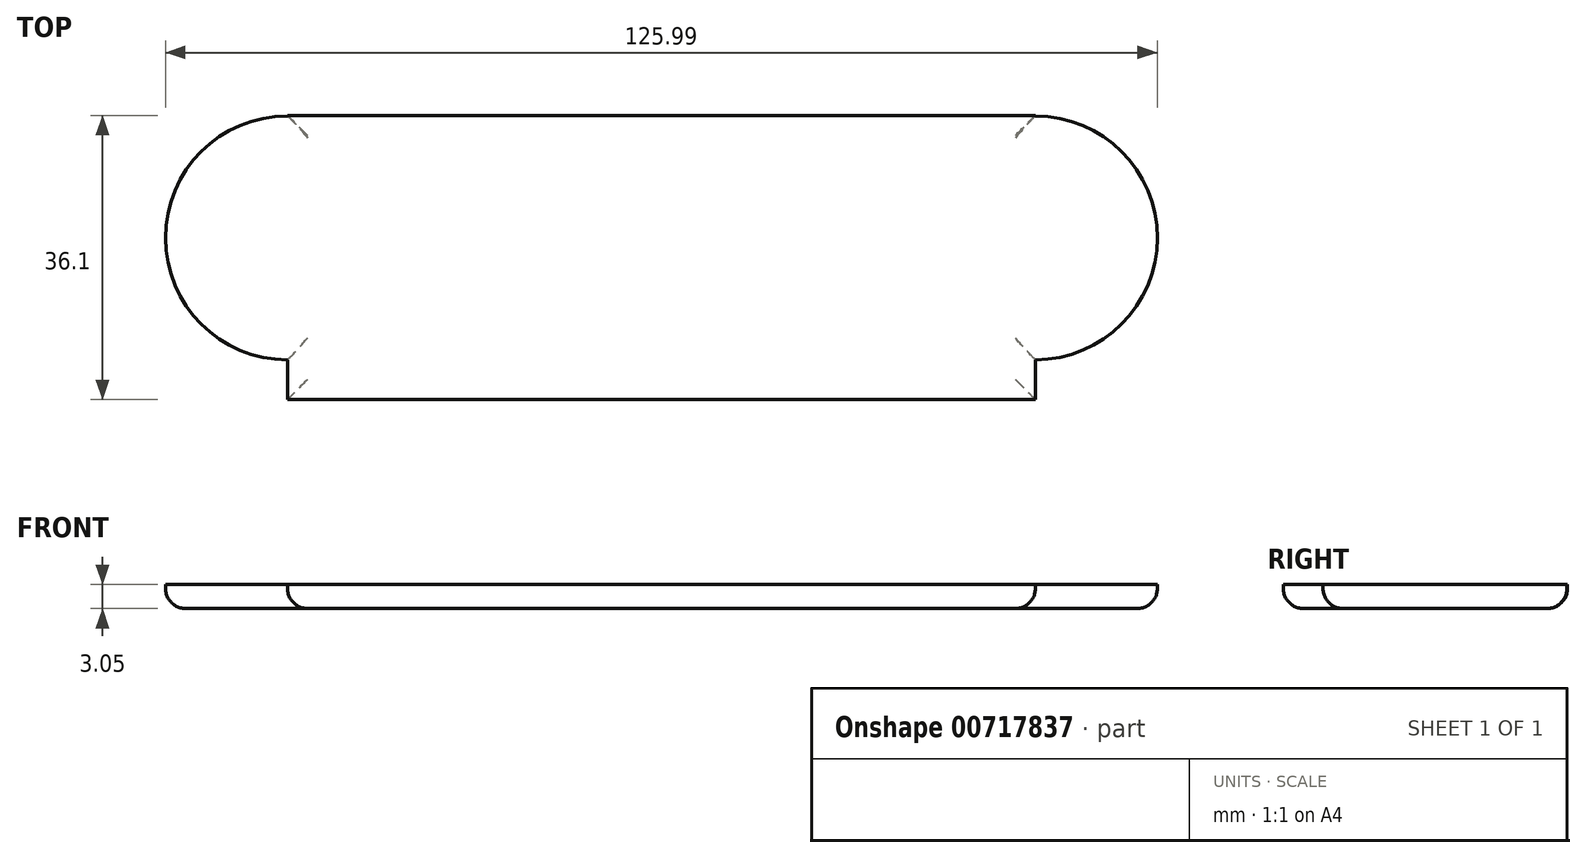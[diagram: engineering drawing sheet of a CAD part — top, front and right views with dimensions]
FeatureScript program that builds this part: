
annotation { "Feature Type Name" : "Feature", "Feature Type Description" : "" }
export const myFeature = defineFeature(function(context is Context, id is Id, definition is map)
    precondition{}
    {
        {
            var Q0;
            Q0=qCreatedBy(makeId("Top.planeOp"),FACE);
            var sketch = newSketch(context, id + "F0", { "sketchPlane" : qUnion([Q0])});
            skLineSegment(sketch, "E0.bottom", {"start": v(47.5, 18.05) * mm, "end": v(-47.5, 18.05) * mm});
            skLineSegment(sketch, "E0.top", {"start": v(47.5, -18.05) * mm, "end": v(-47.5, -18.05) * mm});
            skLineSegment(sketch, "E0.left", {"start": v(47.5, 18.05) * mm, "end": v(47.5, -18.05) * mm});
            skLineSegment(sketch, "E0.right", {"start": v(-47.5, 18.05) * mm, "end": v(-47.5, -18.05) * mm});
            skPoint(sketch, "E0.middle", {"position": v(0, 0) * mm});
            skCircle(sketch, "E1", {"center": v(-47.5, 2.49) * mm, "radius": 15.5 * mm});
            skCircle(sketch, "E2", {"center": v(47.5, 2.49) * mm, "radius": 15.5 * mm});
            skSolve(sketch);
        }
        {
            var Q0;
            Q0=qSketchRegion(id+"F0",true);
            extrude(context, id + "F1", {"entities" : qUnion([Q0]), "oppositeDirection" : true, "depth" : 3.05 * mm, "offsetDistance" : 25.4 * mm});
        }
        {
            var Q0;
            Q0=makeQuery(id+"F1.opExtrude","CAP_EDGE",EDGE,{"disambiguationData":[OSD([sQuery(id+"F0.wireOp",EDGE,"E1")])],"isStart":false});
            var Q1;
            Q1=makeQuery(id+"F1.opExtrude","CAP_EDGE",EDGE,{"disambiguationData":[OSD([sQuery(id+"F0.wireOp",EDGE,"E2")])],"isStart":false});
            var Q2;
            Q2=makeQuery(id+"F1.opExtrude","CAP_FACE",FACE,{"disambiguationData":[OSD([sQuery(id+"F0.wireOp",EDGE,"E0.bottom"),sQuery(id+"F0.wireOp",EDGE,"E0.top"),sQuery(id+"F0.wireOp",EDGE,"E0.left"),sQuery(id+"F0.wireOp",EDGE,"E0.right"),sQuery(id+"F0.wireOp",EDGE,"E1"),sQuery(id+"F0.wireOp",EDGE,"E2")])],"isStart":false});
            fillet(context, id + "F2", {"entities" : qUnion([Q0, Q1, Q2]), "radius" : 2.54 * mm, "tangentPropagation" : true, "allowEdgeOverflow" : false});
        }
    });
